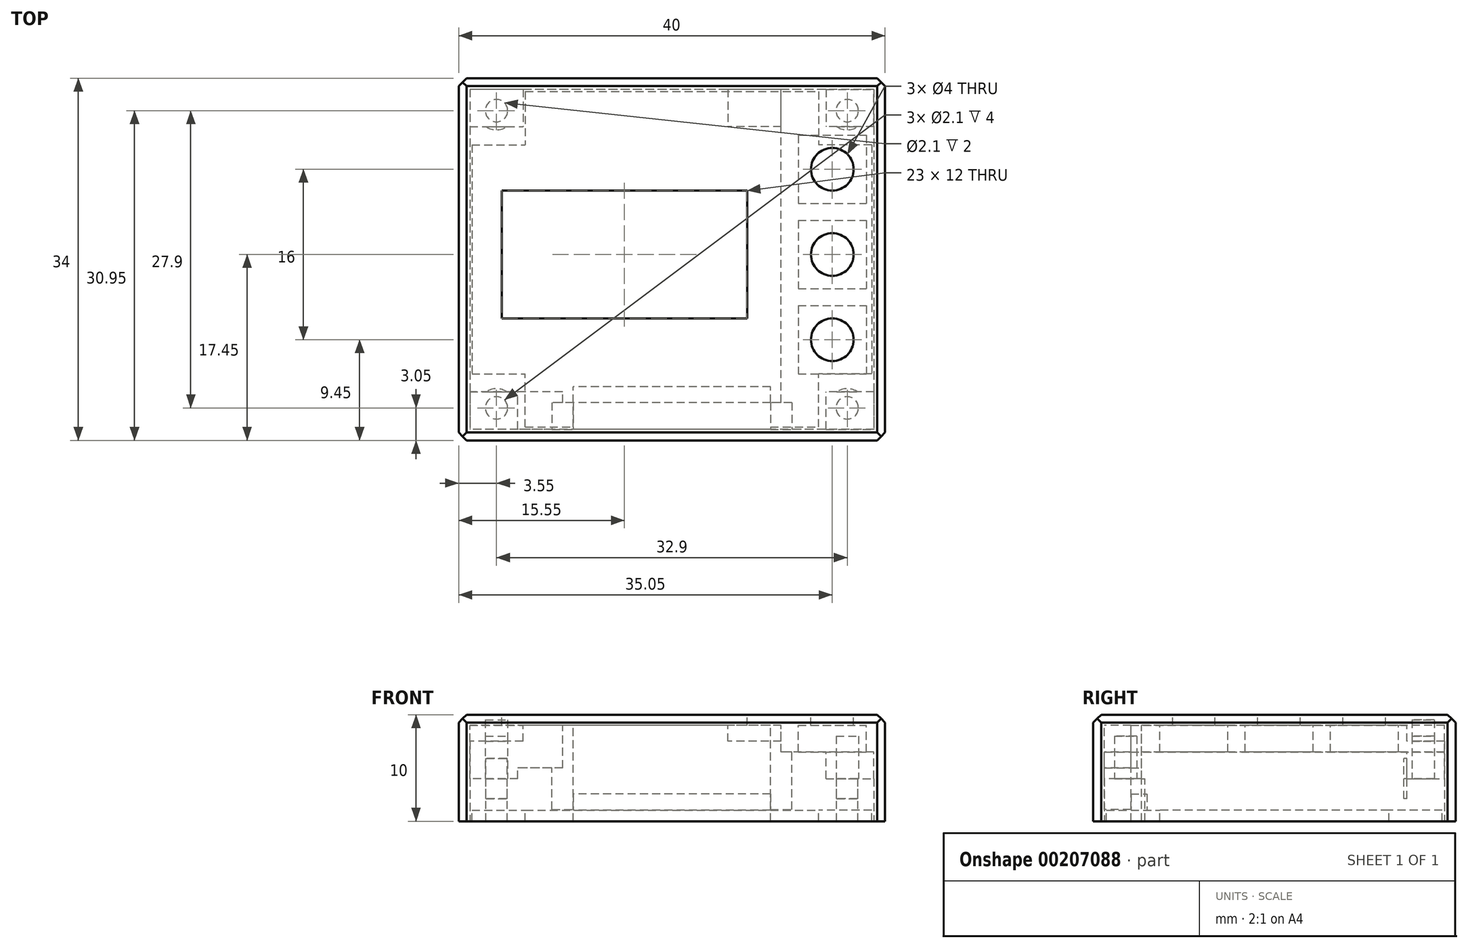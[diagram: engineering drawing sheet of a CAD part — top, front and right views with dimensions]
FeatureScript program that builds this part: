
annotation { "Feature Type Name" : "Feature", "Feature Type Description" : "" }
export const myFeature = defineFeature(function(context is Context, id is Id, definition is map)
    precondition{}
    {
        {
            var Q0;
            Q0=qCreatedBy(makeId("Top.planeOp"),FACE);
            var sketch = newSketch(context, id + "F0", { "sketchPlane" : qUnion([Q0])});
            skLineSegment(sketch, "E0.bottom", {"start": v(20, -17) * mm, "end": v(-20, -17) * mm});
            skLineSegment(sketch, "E0.top", {"start": v(20, 17) * mm, "end": v(-20, 17) * mm});
            skLineSegment(sketch, "E0.left", {"start": v(20, -17) * mm, "end": v(20, 17) * mm});
            skLineSegment(sketch, "E0.right", {"start": v(-20, -17) * mm, "end": v(-20, 17) * mm});
            skPoint(sketch, "E0.middle", {"position": v(0, 0) * mm});
            skSolve(sketch);
        }
        {
            var Q0;
            Q0=makeQuery(id+"F0.imprint","IMPRINT",FACE,{"disambiguationData":[TD([[makeQuery(id+"F0.imprint","IMPRINT",EDGE,{"derivedFrom":sQuery(id+"F0.wireOp",EDGE,"E0.bottom")}),-1.0]])]});
            extrude(context, id + "F1", {"entities" : qUnion([Q0]), "depth" : 10 * mm});
        }
        {
            var Q0;
            Q0=makeQuery(id+"F1.opExtrude","CAP_FACE",FACE,{"disambiguationData":[OSD([sQuery(id+"F0.wireOp",EDGE,"E0.bottom"),sQuery(id+"F0.wireOp",EDGE,"E0.top"),sQuery(id+"F0.wireOp",EDGE,"E0.left"),sQuery(id+"F0.wireOp",EDGE,"E0.right")])],"isStart":true});
            var sketch = newSketch(context, id + "F2", { "sketchPlane" : qUnion([Q0])});
            skLineSegment(sketch, "E1.bottom", {"start": v(18.95, -15.95) * mm, "end": v(-18.95, -15.95) * mm});
            skLineSegment(sketch, "E1.top", {"start": v(18.95, 15.95) * mm, "end": v(-18.95, 15.95) * mm});
            skLineSegment(sketch, "E1.left", {"start": v(18.95, -15.95) * mm, "end": v(18.95, 15.95) * mm});
            skLineSegment(sketch, "E1.right", {"start": v(-18.95, -15.95) * mm, "end": v(-18.95, 15.95) * mm});
            skPoint(sketch, "E1.middle", {"position": v(0, 0) * mm});
            skSolve(sketch);
        }
        {
            var Q0;
            Q0=makeQuery(id+"F2.imprint","IMPRINT",FACE,{"disambiguationData":[TD([[makeQuery(id+"F2.imprint","IMPRINT",EDGE,{"derivedFrom":sQuery(id+"F2.wireOp",EDGE,"E1.bottom")}),-1.0]])]});
            extrude(context, id + "F3", {"entities" : qUnion([Q0]), "operationType" : NewBodyOperationType.REMOVE, "oppositeDirection" : true, "depth" : 9 * mm});
        }
        {
            var Q0;
            Q0=makeQuery(id+"F1.opExtrude","CAP_FACE",FACE,{"disambiguationData":[OSD([sQuery(id+"F0.wireOp",EDGE,"E0.bottom"),sQuery(id+"F0.wireOp",EDGE,"E0.top"),sQuery(id+"F0.wireOp",EDGE,"E0.left"),sQuery(id+"F0.wireOp",EDGE,"E0.right")])],"isStart":false});
            var sketch = newSketch(context, id + "F4", { "sketchPlane" : qUnion([Q0])});
            skLineSegment(sketch, "E2.bottom", {"start": v(-15.95, 6.45) * mm, "end": v(7.05, 6.45) * mm});
            skLineSegment(sketch, "E2.top", {"start": v(-15.95, -5.55) * mm, "end": v(7.05, -5.55) * mm});
            skLineSegment(sketch, "E2.left", {"start": v(-15.95, 6.45) * mm, "end": v(-15.95, -5.55) * mm});
            skLineSegment(sketch, "E2.right", {"start": v(7.05, 6.45) * mm, "end": v(7.05, -5.55) * mm});
            skCircle(sketch, "E3", {"center": v(15.05, 0.45) * mm, "radius": 2 * mm});
            skPoint(sketch, "E3.centerSnap0", {"position": v(7.05, 0.45) * mm});
            skCircle(sketch, "E4", {"center": v(15.05, -7.55) * mm, "radius": 2 * mm});
            skCircle(sketch, "E5", {"center": v(15.05, 8.45) * mm, "radius": 2 * mm});
            skSolve(sketch);
        }
        {
            var Q0;
            Q0=makeQuery(id+"F4.imprint","IMPRINT",FACE,{"disambiguationData":[TD([[makeQuery(id+"F4.imprint","IMPRINT",EDGE,{"derivedFrom":sQuery(id+"F4.wireOp",EDGE,"E4")}),1.0]])]});
            var Q1;
            Q1=makeQuery(id+"F4.imprint","IMPRINT",FACE,{"disambiguationData":[TD([[makeQuery(id+"F4.imprint","IMPRINT",EDGE,{"derivedFrom":sQuery(id+"F4.wireOp",EDGE,"E3")}),1.0]])]});
            var Q2;
            Q2=makeQuery(id+"F4.imprint","IMPRINT",FACE,{"disambiguationData":[TD([[makeQuery(id+"F4.imprint","IMPRINT",EDGE,{"derivedFrom":sQuery(id+"F4.wireOp",EDGE,"E5")}),1.0]])]});
            var Q3;
            Q3=makeQuery(id+"F4.imprint","IMPRINT",FACE,{"disambiguationData":[TD([[makeQuery(id+"F4.imprint","IMPRINT",EDGE,{"derivedFrom":sQuery(id+"F4.wireOp",EDGE,"E2.bottom")}),-1.0]])]});
            extrude(context, id + "F5", {"entities" : qUnion([Q0, Q1, Q2, Q3]), "operationType" : NewBodyOperationType.REMOVE, "oppositeDirection" : true, "depth" : 25 * mm});
        }
        {
            var Q0;
            Q0=makeQuery(id+"F3.boolean.opBoolean","COPY",FACE,{"derivedFrom":makeQuery(id+"F3.opExtrude","CAP_FACE",FACE,{"disambiguationData":[OSD([sQuery(id+"F2.wireOp",EDGE,"E1.bottom"),sQuery(id+"F2.wireOp",EDGE,"E1.top"),sQuery(id+"F2.wireOp",EDGE,"E1.left"),sQuery(id+"F2.wireOp",EDGE,"E1.right")])],"isStart":false})});
            var sketch = newSketch(context, id + "F6", { "sketchPlane" : qUnion([Q0])});
            skLineSegment(sketch, "E6.bottom", {"start": v(11.85, 4.35) * mm, "end": v(18.25, 4.35) * mm});
            skLineSegment(sketch, "E6.top", {"start": v(11.85, 10.75) * mm, "end": v(18.25, 10.75) * mm});
            skLineSegment(sketch, "E6.left", {"start": v(11.85, 4.35) * mm, "end": v(11.85, 10.75) * mm});
            skLineSegment(sketch, "E6.right", {"start": v(18.25, 4.35) * mm, "end": v(18.25, 10.75) * mm});
            skPoint(sketch, "E6.middle", {"position": v(15.05, 7.55) * mm});
            skLineSegment(sketch, "E7.bottom", {"start": v(11.85, -3.65) * mm, "end": v(18.25, -3.65) * mm});
            skLineSegment(sketch, "E7.top", {"start": v(11.85, 2.75) * mm, "end": v(18.25, 2.75) * mm});
            skLineSegment(sketch, "E7.left", {"start": v(11.85, -3.65) * mm, "end": v(11.85, 2.75) * mm});
            skLineSegment(sketch, "E7.right", {"start": v(18.25, -3.65) * mm, "end": v(18.25, 2.75) * mm});
            skPoint(sketch, "E7.middle", {"position": v(15.05, -0.45) * mm});
            skLineSegment(sketch, "E8.bottom", {"start": v(11.85, -11.65) * mm, "end": v(18.25, -11.65) * mm});
            skLineSegment(sketch, "E8.top", {"start": v(11.85, -5.25) * mm, "end": v(18.25, -5.25) * mm});
            skLineSegment(sketch, "E8.left", {"start": v(11.85, -11.65) * mm, "end": v(11.85, -5.25) * mm});
            skLineSegment(sketch, "E8.right", {"start": v(18.25, -11.65) * mm, "end": v(18.25, -5.25) * mm});
            skPoint(sketch, "E8.middle", {"position": v(15.05, -8.45) * mm});
            skLineSegment(sketch, "E9", {"start": v(10.25, 15.95) * mm, "end": v(10.25, -15.95) * mm});
            skLineSegment(sketch, "E10", {"start": v(10.25, 12.45) * mm, "end": v(-18.95, 12.45) * mm});
            skLineSegment(sketch, "E11", {"start": v(-10.25, 15.95) * mm, "end": v(-10.25, 12.45) * mm});
            skLineSegment(sketch, "E12.bottom", {"start": v(-18.95, 12.45) * mm, "end": v(-13.95, 12.45) * mm});
            skLineSegment(sketch, "E12.top", {"start": v(-18.95, 8.95) * mm, "end": v(-13.95, 8.95) * mm});
            skLineSegment(sketch, "E12.left", {"start": v(-18.95, 12.45) * mm, "end": v(-18.95, 8.95) * mm});
            skLineSegment(sketch, "E12.right", {"start": v(-13.95, 12.45) * mm, "end": v(-13.95, 8.95) * mm});
            skLineSegment(sketch, "E13.bottom", {"start": v(-18.95, -15.95) * mm, "end": v(-13.95, -15.95) * mm});
            skLineSegment(sketch, "E13.top", {"start": v(-18.95, -12.45) * mm, "end": v(-13.95, -12.45) * mm});
            skLineSegment(sketch, "E13.left", {"start": v(-18.95, -15.95) * mm, "end": v(-18.95, -12.45) * mm});
            skLineSegment(sketch, "E13.right", {"start": v(-13.95, -15.95) * mm, "end": v(-13.95, -12.45) * mm});
            skLineSegment(sketch, "E14.bottom", {"start": v(10.25, -15.95) * mm, "end": v(5.25, -15.95) * mm});
            skLineSegment(sketch, "E14.top", {"start": v(10.25, -12.45) * mm, "end": v(5.25, -12.45) * mm});
            skLineSegment(sketch, "E14.left", {"start": v(10.25, -15.95) * mm, "end": v(10.25, -12.45) * mm});
            skLineSegment(sketch, "E14.right", {"start": v(5.25, -15.95) * mm, "end": v(5.25, -12.45) * mm});
            skLineSegment(sketch, "E15.bottom", {"start": v(10.25, 12.45) * mm, "end": v(5.25, 12.45) * mm});
            skLineSegment(sketch, "E15.top", {"start": v(10.25, 8.95) * mm, "end": v(5.25, 8.95) * mm});
            skLineSegment(sketch, "E15.left", {"start": v(10.25, 12.45) * mm, "end": v(10.25, 8.95) * mm});
            skLineSegment(sketch, "E15.right", {"start": v(5.25, 12.45) * mm, "end": v(5.25, 8.95) * mm});
            skSolve(sketch);
        }
        {
            var Q0;
            Q0=makeQuery(id+"F6.imprint","IMPRINT",FACE,{"disambiguationData":[TD([[makeQuery(id+"F6.imprint","IMPRINT",EDGE,{"derivedFrom":sQuery(id+"F6.wireOp",EDGE,"E6.bottom")}),-1.0]])]});
            extrude(context, id + "F7", {"entities" : qUnion([Q0]), "operationType" : NewBodyOperationType.ADD, "depth" : 2.5 * mm});
        }
        {
            var Q0;
            Q0=makeQuery(id+"F6.imprint","IMPRINT",FACE,{"disambiguationData":[TD([[makeQuery(id+"F6.imprint","IMPRINT",EDGE,{"derivedFrom":sQuery(id+"F6.wireOp",EDGE,"E12.bottom")}),-1.0]])]});
            var Q1;
            Q1=makeQuery(id+"F6.imprint","IMPRINT",FACE,{"disambiguationData":[TD([[makeQuery(id+"F6.imprint","IMPRINT",EDGE,{"derivedFrom":sQuery(id+"F6.wireOp",EDGE,"E15.bottom")}),1.0]])]});
            var Q2;
            Q2=makeQuery(id+"F6.imprint","IMPRINT",FACE,{"disambiguationData":[TD([[makeQuery(id+"F6.imprint","IMPRINT",EDGE,{"derivedFrom":sQuery(id+"F6.wireOp",EDGE,"E13.bottom")}),-1.0]])]});
            var Q3;
            Q3=makeQuery(id+"F6.imprint","IMPRINT",FACE,{"disambiguationData":[TD([[makeQuery(id+"F6.imprint","IMPRINT",EDGE,{"derivedFrom":sQuery(id+"F6.wireOp",EDGE,"E14.bottom")}),-1.0]])]});
            extrude(context, id + "F8", {"entities" : qUnion([Q0, Q1, Q2, Q3]), "operationType" : NewBodyOperationType.ADD, "depth" : 1.5 * mm});
        }
        {
            var Q0;
            {var subQ3=sQuery(id+"F6.wireOp",EDGE,"E11");Q0=makeQuery(id+"F6.imprint","IMPRINT",FACE,{"disambiguationData":[TD([[makeQuery(id+"F6.imprint","IMPRINT",EDGE,{"derivedFrom":subQ3}),-1.0]])]});}
            extrude(context, id + "F9", {"entities" : qUnion([Q0]), "operationType" : NewBodyOperationType.ADD, "depth" : 4 * mm});
        }
        {
            var Q0;
            Q0=makeQuery(id+"F8.opExtrude","CAP_FACE",FACE,{"disambiguationData":[OSD([sQuery(id+"F6.wireOp",EDGE,"E13.bottom"),sQuery(id+"F6.wireOp",EDGE,"E13.top"),sQuery(id+"F6.wireOp",EDGE,"E13.left"),sQuery(id+"F6.wireOp",EDGE,"E13.right")])],"isStart":false});
            var sketch = newSketch(context, id + "F10", { "sketchPlane" : qUnion([Q0])});
            skCircle(sketch, "E16", {"center": v(-16.45, -13.95) * mm, "radius": 1.05 * mm});
            skSolve(sketch);
        }
        {
            var Q0;
            Q0=makeQuery(id+"F10.imprint","IMPRINT",FACE,{"disambiguationData":[TD([[makeQuery(id+"F10.imprint","IMPRINT",EDGE,{"derivedFrom":sQuery(id+"F10.wireOp",EDGE,"E16")}),1.0]])]});
            extrude(context, id + "F11", {"entities" : qUnion([Q0]), "operationType" : NewBodyOperationType.REMOVE, "oppositeDirection" : true, "depth" : 2 * mm});
        }
        {
            var Q0;
            Q0=makeQuery(id+"F1.opExtrude","CAP_EDGE",EDGE,{"disambiguationData":[OSD([sQuery(id+"F0.wireOp",EDGE,"E0.right")])],"isStart":false});
            var Q1;
            Q1=makeQuery(id+"F1.opExtrude","CAP_EDGE",EDGE,{"disambiguationData":[OSD([sQuery(id+"F0.wireOp",EDGE,"E0.top")])],"isStart":false});
            var Q2;
            Q2=makeQuery(id+"F1.opExtrude","CAP_EDGE",EDGE,{"disambiguationData":[OSD([sQuery(id+"F0.wireOp",EDGE,"E0.left")])],"isStart":false});
            var Q3;
            Q3=makeQuery(id+"F1.opExtrude","CAP_EDGE",EDGE,{"disambiguationData":[OSD([sQuery(id+"F0.wireOp",EDGE,"E0.bottom")])],"isStart":false});
            var Q4;
            Q4=makeQuery(id+"F5.boolean.opBoolean","COPY",EDGE,{"derivedFrom":makeQuery(id+"F5.opExtrude","CAP_EDGE",EDGE,{"disambiguationData":[OSD([sQuery(id+"F4.wireOp",EDGE,"E2.bottom")])],"isStart":true})});
            var Q5;
            Q5=makeQuery(id+"F5.boolean.opBoolean","COPY",EDGE,{"derivedFrom":makeQuery(id+"F5.opExtrude","CAP_EDGE",EDGE,{"disambiguationData":[OSD([sQuery(id+"F4.wireOp",EDGE,"E2.right")])],"isStart":true})});
            var Q6;
            Q6=makeQuery(id+"F5.boolean.opBoolean","COPY",EDGE,{"derivedFrom":makeQuery(id+"F5.opExtrude","CAP_EDGE",EDGE,{"disambiguationData":[OSD([sQuery(id+"F4.wireOp",EDGE,"E2.top")])],"isStart":true})});
            var Q7;
            Q7=makeQuery(id+"F5.boolean.opBoolean","COPY",EDGE,{"derivedFrom":makeQuery(id+"F5.opExtrude","CAP_EDGE",EDGE,{"disambiguationData":[OSD([sQuery(id+"F4.wireOp",EDGE,"E2.left")])],"isStart":true})});
            var Q8;
            Q8=makeQuery(id+"F5.boolean.opBoolean","COPY",EDGE,{"derivedFrom":makeQuery(id+"F5.opExtrude","CAP_EDGE",EDGE,{"disambiguationData":[OSD([sQuery(id+"F4.wireOp",EDGE,"E5")])],"isStart":true})});
            var Q9;
            Q9=makeQuery(id+"F5.boolean.opBoolean","COPY",EDGE,{"derivedFrom":makeQuery(id+"F5.opExtrude","CAP_EDGE",EDGE,{"disambiguationData":[OSD([sQuery(id+"F4.wireOp",EDGE,"E3")])],"isStart":true})});
            var Q10;
            Q10=makeQuery(id+"F5.boolean.opBoolean","COPY",EDGE,{"derivedFrom":makeQuery(id+"F5.opExtrude","CAP_EDGE",EDGE,{"disambiguationData":[OSD([sQuery(id+"F4.wireOp",EDGE,"E4")])],"isStart":true})});
            chamfer(context, id + "F12", {"entities" : qUnion([Q0, Q1, Q2, Q3, Q4, Q5, Q6, Q7, Q8, Q9, Q10]), "width" : 0.75 * mm, "tangentPropagation" : true});
        }
        {
            var Q0;
            Q0=makeQuery(id+"F3.boolean.opBoolean","COPY",FACE,{"derivedFrom":makeQuery(id+"F3.opExtrude","SWEPT_FACE",FACE,{"disambiguationData":[OSD([sQuery(id+"F2.wireOp",EDGE,"E1.top")])]})});
            var sketch = newSketch(context, id + "F13", { "sketchPlane" : qUnion([Q0])});
            skLineSegment(sketch, "E17", {"start": v(11.25, 0) * mm, "end": v(11.25, 9) * mm});
            skLineSegment(sketch, "E18", {"start": v(9.25, 0) * mm, "end": v(9.25, 9) * mm});
            skLineSegment(sketch, "E19.bottom", {"start": v(-9.25, 0) * mm, "end": v(-11.25, 0) * mm});
            skLineSegment(sketch, "E19.top", {"start": v(-9.25, 9) * mm, "end": v(-11.25, 9) * mm});
            skLineSegment(sketch, "E19.left", {"start": v(-9.25, 0) * mm, "end": v(-9.25, 9) * mm});
            skLineSegment(sketch, "E19.right", {"start": v(-11.25, 0) * mm, "end": v(-11.25, 9) * mm});
            skSolve(sketch);
        }
        {
            var Q0;
            {var subQ4=sQuery(id+"F13.wireOp",EDGE,"E18");Q0=makeQuery(id+"F13.imprint","IMPRINT",FACE,{"disambiguationData":[TD([[makeQuery(id+"F13.imprint","IMPRINT",EDGE,{"derivedFrom":subQ4}),-1.0]])]});}
            var Q1;
            {var subQ1=sQuery(id+"F13.wireOp",EDGE,"E19.bottom");Q1=makeQuery(id+"F13.imprint","IMPRINT",FACE,{"disambiguationData":[TD([[makeQuery(id+"F13.imprint","IMPRINT",EDGE,{"derivedFrom":subQ1}),1.0]])]});}
            extrude(context, id + "F14", {"entities" : qUnion([Q0, Q1]), "operationType" : NewBodyOperationType.ADD, "depth" : 2.5 * mm});
        }
        {
            var Q0;
            {var subQ0=sQuery(id+"F2.wireOp",EDGE,"E1.top");var subQ1=makeQuery(id+"F3.boolean.opBoolean","COPY",EDGE,{"derivedFrom":makeQuery(id+"F3.opExtrude","CAP_EDGE",EDGE,{"disambiguationData":[OSD([subQ0])],"isStart":true})});Q0=makeQuery(id+"F14.boolean.opBoolean","MERGE",FACE,{"derivedFrom":[makeQuery(id+"F1.opExtrude","CAP_FACE",FACE,{"disambiguationData":[OSD([sQuery(id+"F0.wireOp",EDGE,"E0.bottom"),sQuery(id+"F0.wireOp",EDGE,"E0.top"),sQuery(id+"F0.wireOp",EDGE,"E0.left"),sQuery(id+"F0.wireOp",EDGE,"E0.right")])],"isStart":true}),makeQuery(id+"F14.opExtrude","SWEPT_FACE",FACE,{"disambiguationData":[OSD([sQuery(id+"F13.wireOp",EDGE,"E19.bottom")])]}),makeQuery(id+"F14.opExtrude","SWEPT_FACE",FACE,{"disambiguationData":[OSD([subQ0]),TDD([makeQuery(id+"F13.imprint","IMPRINT",EDGE,{"disambiguationData":[TD([[makeQuery(id+"F13.imprint","INTERSECT",VERTEX,{"derivedFrom":[subQ1,sQuery(id+"F13.wireOp",EDGE,"E17")]}),1.0]])],"derivedFrom":subQ1})])]})]});}
            var sketch = newSketch(context, id + "F15", { "sketchPlane" : qUnion([Q0])});
            skLineSegment(sketch, "E20", {"start": v(-11.25, 15.95) * mm, "end": v(-9.25, 15.95) * mm});
            skLineSegment(sketch, "E21", {"start": v(9.25, 15.95) * mm, "end": v(11.25, 15.95) * mm});
            skSolve(sketch);
        }
        {
            var Q0;
            Q0=makeQuery(id+"F15.imprint","IMPRINT",FACE,{"disambiguationData":[TD([[makeQuery(id+"F15.imprint","IMPRINT",EDGE,{"derivedFrom":sQuery(id+"F15.wireOp",EDGE,"E20")}),-1.0]])]});
            var Q1;
            Q1=makeQuery(id+"F15.imprint","IMPRINT",FACE,{"disambiguationData":[TD([[makeQuery(id+"F15.imprint","IMPRINT",EDGE,{"derivedFrom":sQuery(id+"F15.wireOp",EDGE,"E21")}),-1.0]])]});
            extrude(context, id + "F16", {"entities" : qUnion([Q0, Q1]), "operationType" : NewBodyOperationType.REMOVE, "oppositeDirection" : true, "depth" : 1.1 * mm});
        }
        {
            var Q0;
            Q0=makeQuery(id+"F1.opExtrude","SWEPT_EDGE",EDGE,{"disambiguationData":[OSD([sQuery(id+"F0.wireOp",EDGE,"E0.top"),sQuery(id+"F0.wireOp",EDGE,"E0.right")])]});
            var Q1;
            Q1=makeQuery(id+"F1.opExtrude","SWEPT_EDGE",EDGE,{"disambiguationData":[OSD([sQuery(id+"F0.wireOp",EDGE,"E0.top"),sQuery(id+"F0.wireOp",EDGE,"E0.left")])]});
            var Q2;
            Q2=makeQuery(id+"F1.opExtrude","SWEPT_EDGE",EDGE,{"disambiguationData":[OSD([sQuery(id+"F0.wireOp",EDGE,"E0.bottom"),sQuery(id+"F0.wireOp",EDGE,"E0.right")])]});
            var Q3;
            Q3=makeQuery(id+"F1.opExtrude","SWEPT_EDGE",EDGE,{"disambiguationData":[OSD([sQuery(id+"F0.wireOp",EDGE,"E0.bottom"),sQuery(id+"F0.wireOp",EDGE,"E0.left")])]});
            chamfer(context, id + "F17", {"entities" : qUnion([Q0, Q1, Q2, Q3]), "width" : 0.75 * mm, "tangentPropagation" : true});
        }
        {
            var Q0;
            Q0=makeQuery(id+"F9.opExtrude","CAP_FACE",FACE,{"disambiguationData":[OSD([sQuery(id+"F2.wireOp",EDGE,"E1.top"),sQuery(id+"F2.wireOp",EDGE,"E1.right"),sQuery(id+"F6.wireOp",EDGE,"E10"),sQuery(id+"F6.wireOp",EDGE,"E11"),sQuery(id+"F6.wireOp",EDGE,"E12.bottom")])],"isStart":false});
            var sketch = newSketch(context, id + "F18", { "sketchPlane" : qUnion([Q0])});
            skLineSegment(sketch, "E22.bottom", {"start": v(-18.95, 15.95) * mm, "end": v(-14.45, 15.95) * mm});
            skLineSegment(sketch, "E22.top", {"start": v(-18.95, 12.45) * mm, "end": v(-14.45, 12.45) * mm});
            skLineSegment(sketch, "E22.left", {"start": v(-18.95, 15.95) * mm, "end": v(-18.95, 12.45) * mm});
            skLineSegment(sketch, "E22.right", {"start": v(-14.45, 15.95) * mm, "end": v(-14.45, 12.45) * mm});
            skSolve(sketch);
        }
        {
            var Q0;
            Q0=makeQuery(id+"F7.opExtrude","CAP_FACE",FACE,{"disambiguationData":[OSD([sQuery(id+"F2.wireOp",EDGE,"E1.bottom"),sQuery(id+"F2.wireOp",EDGE,"E1.top"),sQuery(id+"F2.wireOp",EDGE,"E1.left"),sQuery(id+"F6.wireOp",EDGE,"E6.bottom"),sQuery(id+"F6.wireOp",EDGE,"E6.top"),sQuery(id+"F6.wireOp",EDGE,"E6.left"),sQuery(id+"F6.wireOp",EDGE,"E6.right"),sQuery(id+"F6.wireOp",EDGE,"E7.bottom"),sQuery(id+"F6.wireOp",EDGE,"E7.top"),sQuery(id+"F6.wireOp",EDGE,"E7.left"),sQuery(id+"F6.wireOp",EDGE,"E7.right"),sQuery(id+"F6.wireOp",EDGE,"E8.bottom"),sQuery(id+"F6.wireOp",EDGE,"E8.top"),sQuery(id+"F6.wireOp",EDGE,"E8.left"),sQuery(id+"F6.wireOp",EDGE,"E8.right"),sQuery(id+"F6.wireOp",EDGE,"E9"),sQuery(id+"F6.wireOp",EDGE,"E14.left"),sQuery(id+"F6.wireOp",EDGE,"E15.left")])],"isStart":false});
            var sketch = newSketch(context, id + "F19", { "sketchPlane" : qUnion([Q0])});
            skLineSegment(sketch, "E23.bottom", {"start": v(18.95, 15.95) * mm, "end": v(14.45, 15.95) * mm});
            skLineSegment(sketch, "E23.top", {"start": v(18.95, 12.45) * mm, "end": v(14.45, 12.45) * mm});
            skLineSegment(sketch, "E23.left", {"start": v(18.95, 15.95) * mm, "end": v(18.95, 12.45) * mm});
            skLineSegment(sketch, "E23.right", {"start": v(14.45, 15.95) * mm, "end": v(14.45, 12.45) * mm});
            skLineSegment(sketch, "E24.bottom", {"start": v(18.95, -15.95) * mm, "end": v(14.45, -15.95) * mm});
            skLineSegment(sketch, "E24.top", {"start": v(18.95, -12.45) * mm, "end": v(14.45, -12.45) * mm});
            skLineSegment(sketch, "E24.left", {"start": v(18.95, -15.95) * mm, "end": v(18.95, -12.45) * mm});
            skLineSegment(sketch, "E24.right", {"start": v(14.45, -15.95) * mm, "end": v(14.45, -12.45) * mm});
            skSolve(sketch);
        }
        {
            var Q0;
            Q0=makeQuery(id+"F18.imprint","IMPRINT",FACE,{"disambiguationData":[TD([[makeQuery(id+"F18.imprint","IMPRINT",EDGE,{"derivedFrom":sQuery(id+"F18.wireOp",EDGE,"E22.bottom")}),1.0]])]});
            var Q1;
            Q1=makeQuery(id+"F19.imprint","IMPRINT",FACE,{"disambiguationData":[TD([[makeQuery(id+"F19.imprint","IMPRINT",EDGE,{"derivedFrom":sQuery(id+"F19.wireOp",EDGE,"E23.bottom")}),1.0]])]});
            var Q2;
            Q2=makeQuery(id+"F19.imprint","IMPRINT",FACE,{"disambiguationData":[TD([[makeQuery(id+"F19.imprint","IMPRINT",EDGE,{"derivedFrom":sQuery(id+"F19.wireOp",EDGE,"E24.bottom")}),-1.0]])]});
            var Q3;
            {var subQ0=sQuery(id+"F2.wireOp",EDGE,"E1.top");var subQ1=makeQuery(id+"F3.boolean.opBoolean","COPY",EDGE,{"derivedFrom":makeQuery(id+"F3.opExtrude","CAP_EDGE",EDGE,{"disambiguationData":[OSD([subQ0])],"isStart":true})});Q3=makeQuery(id+"F14.boolean.opBoolean","MERGE",FACE,{"derivedFrom":[makeQuery(id+"F1.opExtrude","CAP_FACE",FACE,{"disambiguationData":[OSD([sQuery(id+"F0.wireOp",EDGE,"E0.bottom"),sQuery(id+"F0.wireOp",EDGE,"E0.top"),sQuery(id+"F0.wireOp",EDGE,"E0.left"),sQuery(id+"F0.wireOp",EDGE,"E0.right")])],"isStart":true}),makeQuery(id+"F14.opExtrude","SWEPT_FACE",FACE,{"disambiguationData":[OSD([sQuery(id+"F13.wireOp",EDGE,"E19.bottom")])]}),makeQuery(id+"F14.opExtrude","SWEPT_FACE",FACE,{"disambiguationData":[OSD([subQ0]),TDD([makeQuery(id+"F13.imprint","IMPRINT",EDGE,{"disambiguationData":[TD([[makeQuery(id+"F13.imprint","INTERSECT",VERTEX,{"derivedFrom":[subQ1,sQuery(id+"F13.wireOp",EDGE,"E17")]}),1.0]])],"derivedFrom":subQ1})])]})]});}
            extrude(context, id + "F20", {"entities" : qUnion([Q0, Q1, Q2]), "operationType" : NewBodyOperationType.ADD, "endBound" : BoundingType.UP_TO_SURFACE, "endBoundEntityFace" : qUnion([Q3]), "depth" : 25 * mm});
        }
        {
            var Q0;
            {var subQ0=sQuery(id+"F13.wireOp",EDGE,"E19.bottom");var subQ1=sQuery(id+"F2.wireOp",EDGE,"E1.top");var subQ2=sQuery(id+"F0.wireOp",EDGE,"E0.right");var subQ3=sQuery(id+"F0.wireOp",EDGE,"E0.left");var subQ4=sQuery(id+"F0.wireOp",EDGE,"E0.top");var subQ5=sQuery(id+"F0.wireOp",EDGE,"E0.bottom");var subQ6=makeQuery(id+"F3.boolean.opBoolean","COPY",EDGE,{"derivedFrom":makeQuery(id+"F3.opExtrude","CAP_EDGE",EDGE,{"disambiguationData":[OSD([subQ1])],"isStart":true})});Q0=makeQuery(id+"F20.boolean.opBoolean","MERGE",FACE,{"derivedFrom":[makeQuery(id+"F14.boolean.opBoolean","MERGE",FACE,{"derivedFrom":[makeQuery(id+"F1.opExtrude","CAP_FACE",FACE,{"disambiguationData":[OSD([subQ5,subQ4,subQ3,subQ2])],"isStart":true}),makeQuery(id+"F14.opExtrude","SWEPT_FACE",FACE,{"disambiguationData":[OSD([subQ0])]}),makeQuery(id+"F14.opExtrude","SWEPT_FACE",FACE,{"disambiguationData":[OSD([subQ1]),TDD([makeQuery(id+"F13.imprint","IMPRINT",EDGE,{"disambiguationData":[TD([[makeQuery(id+"F13.imprint","INTERSECT",VERTEX,{"derivedFrom":[subQ6,sQuery(id+"F13.wireOp",EDGE,"E17")]}),1.0]])],"derivedFrom":subQ6})])]})]}),makeQuery(id+"F20.opExtrude","CAP_FACE",FACE,{"disambiguationData":[OSD([subQ5,subQ4,subQ3,subQ2,subQ1,subQ0]),ownerDisambiguation([makeQuery(id+"F20.opExtrude","SWEPT_BODY",BODY,{"disambiguationData":[OSD([sQuery(id+"F18.wireOp",EDGE,"E22.bottom"),sQuery(id+"F18.wireOp",EDGE,"E22.top"),sQuery(id+"F18.wireOp",EDGE,"E22.left"),sQuery(id+"F18.wireOp",EDGE,"E22.right")])]})])],"isStart":false}),makeQuery(id+"F20.opExtrude","CAP_FACE",FACE,{"disambiguationData":[OSD([subQ5,subQ4,subQ3,subQ2,subQ1,subQ0]),ownerDisambiguation([makeQuery(id+"F20.opExtrude","SWEPT_BODY",BODY,{"disambiguationData":[OSD([sQuery(id+"F19.wireOp",EDGE,"E23.bottom"),sQuery(id+"F19.wireOp",EDGE,"E23.top"),sQuery(id+"F19.wireOp",EDGE,"E23.left"),sQuery(id+"F19.wireOp",EDGE,"E23.right")])]})])],"isStart":false}),makeQuery(id+"F20.opExtrude","CAP_FACE",FACE,{"disambiguationData":[OSD([subQ5,subQ4,subQ3,subQ2,subQ1,subQ0]),ownerDisambiguation([makeQuery(id+"F20.opExtrude","SWEPT_BODY",BODY,{"disambiguationData":[OSD([sQuery(id+"F19.wireOp",EDGE,"E24.bottom"),sQuery(id+"F19.wireOp",EDGE,"E24.top"),sQuery(id+"F19.wireOp",EDGE,"E24.left"),sQuery(id+"F19.wireOp",EDGE,"E24.right")])]})])],"isStart":false})]});}
            var sketch = newSketch(context, id + "F21", { "sketchPlane" : qUnion([Q0])});
            skLineSegment(sketch, "E25.bottom", {"start": v(-14.45, 12.45) * mm, "end": v(-18.95, 12.45) * mm});
            skLineSegment(sketch, "E25.top", {"start": v(-14.45, 15.95) * mm, "end": v(-18.95, 15.95) * mm});
            skLineSegment(sketch, "E25.left", {"start": v(-14.45, 12.45) * mm, "end": v(-14.45, 15.95) * mm});
            skLineSegment(sketch, "E25.right", {"start": v(-18.95, 12.45) * mm, "end": v(-18.95, 15.95) * mm});
            skLineSegment(sketch, "E26.bottom", {"start": v(14.45, 12.45) * mm, "end": v(18.95, 12.45) * mm});
            skLineSegment(sketch, "E26.top", {"start": v(14.45, 15.95) * mm, "end": v(18.95, 15.95) * mm});
            skLineSegment(sketch, "E26.left", {"start": v(14.45, 12.45) * mm, "end": v(14.45, 15.95) * mm});
            skLineSegment(sketch, "E26.right", {"start": v(18.95, 12.45) * mm, "end": v(18.95, 15.95) * mm});
            skLineSegment(sketch, "E27.bottom", {"start": v(14.45, -12.45) * mm, "end": v(18.95, -12.45) * mm});
            skLineSegment(sketch, "E27.top", {"start": v(14.45, -15.95) * mm, "end": v(18.95, -15.95) * mm});
            skLineSegment(sketch, "E27.left", {"start": v(14.45, -12.45) * mm, "end": v(14.45, -15.95) * mm});
            skLineSegment(sketch, "E27.right", {"start": v(18.95, -12.45) * mm, "end": v(18.95, -15.95) * mm});
            skSolve(sketch);
        }
        {
            var Q0;
            Q0=makeQuery(id+"F21.imprint","IMPRINT",FACE,{"disambiguationData":[TD([[makeQuery(id+"F21.imprint","IMPRINT",EDGE,{"derivedFrom":sQuery(id+"F21.wireOp",EDGE,"E25.bottom")}),1.0]])]});
            var Q1;
            Q1=makeQuery(id+"F21.imprint","IMPRINT",FACE,{"disambiguationData":[TD([[makeQuery(id+"F21.imprint","IMPRINT",EDGE,{"derivedFrom":sQuery(id+"F21.wireOp",EDGE,"E26.bottom")}),1.0]])]});
            var Q2;
            Q2=makeQuery(id+"F21.imprint","IMPRINT",FACE,{"disambiguationData":[TD([[makeQuery(id+"F21.imprint","IMPRINT",EDGE,{"derivedFrom":sQuery(id+"F21.wireOp",EDGE,"E27.bottom")}),-1.0]])]});
            extrude(context, id + "F22", {"entities" : qUnion([Q0, Q1, Q2]), "operationType" : NewBodyOperationType.REMOVE, "oppositeDirection" : true, "depth" : 4 * mm});
        }
        {
            var Q0;
            Q0=makeQuery(id+"F22.boolean.opBoolean","COPY",FACE,{"derivedFrom":makeQuery(id+"F22.opExtrude","CAP_FACE",FACE,{"disambiguationData":[OSD([sQuery(id+"F21.wireOp",EDGE,"E25.bottom"),sQuery(id+"F21.wireOp",EDGE,"E25.top"),sQuery(id+"F21.wireOp",EDGE,"E25.left"),sQuery(id+"F21.wireOp",EDGE,"E25.right")])],"isStart":false})});
            var sketch = newSketch(context, id + "F23", { "sketchPlane" : qUnion([Q0])});
            skCircle(sketch, "E28", {"center": v(-16.45, 13.95) * mm, "radius": 1.05 * mm});
            skSolve(sketch);
        }
        {
            var Q0;
            Q0=makeQuery(id+"F22.boolean.opBoolean","COPY",FACE,{"derivedFrom":makeQuery(id+"F22.opExtrude","CAP_FACE",FACE,{"disambiguationData":[OSD([sQuery(id+"F21.wireOp",EDGE,"E26.bottom"),sQuery(id+"F21.wireOp",EDGE,"E26.top"),sQuery(id+"F21.wireOp",EDGE,"E26.left"),sQuery(id+"F21.wireOp",EDGE,"E26.right")])],"isStart":false})});
            var sketch = newSketch(context, id + "F24", { "sketchPlane" : qUnion([Q0])});
            skCircle(sketch, "E29", {"center": v(16.45, 13.95) * mm, "radius": 1.05 * mm});
            skSolve(sketch);
        }
        {
            var Q0;
            Q0=makeQuery(id+"F22.boolean.opBoolean","COPY",FACE,{"derivedFrom":makeQuery(id+"F22.opExtrude","CAP_FACE",FACE,{"disambiguationData":[OSD([sQuery(id+"F21.wireOp",EDGE,"E27.bottom"),sQuery(id+"F21.wireOp",EDGE,"E27.top"),sQuery(id+"F21.wireOp",EDGE,"E27.left"),sQuery(id+"F21.wireOp",EDGE,"E27.right")])],"isStart":false})});
            var sketch = newSketch(context, id + "F25", { "sketchPlane" : qUnion([Q0])});
            skCircle(sketch, "E30", {"center": v(16.45, -13.95) * mm, "radius": 1.05 * mm});
            skSolve(sketch);
        }
        {
            var Q0;
            Q0=makeQuery(id+"F23.imprint","IMPRINT",FACE,{"disambiguationData":[TD([[makeQuery(id+"F23.imprint","IMPRINT",EDGE,{"derivedFrom":sQuery(id+"F23.wireOp",EDGE,"E28")}),1.0]])]});
            var Q1;
            Q1=makeQuery(id+"F24.imprint","IMPRINT",FACE,{"disambiguationData":[TD([[makeQuery(id+"F24.imprint","IMPRINT",EDGE,{"derivedFrom":sQuery(id+"F24.wireOp",EDGE,"E29")}),1.0]])]});
            var Q2;
            Q2=makeQuery(id+"F25.imprint","IMPRINT",FACE,{"disambiguationData":[TD([[makeQuery(id+"F25.imprint","IMPRINT",EDGE,{"derivedFrom":sQuery(id+"F25.wireOp",EDGE,"E30")}),1.0]])]});
            extrude(context, id + "F26", {"entities" : qUnion([Q0, Q1, Q2]), "operationType" : NewBodyOperationType.REMOVE, "oppositeDirection" : true, "depth" : 4 * mm});
        }
        {
            var Q0;
            {var subQ0=sQuery(id+"F13.wireOp",EDGE,"E19.bottom");var subQ1=sQuery(id+"F2.wireOp",EDGE,"E1.top");var subQ2=sQuery(id+"F0.wireOp",EDGE,"E0.right");var subQ3=sQuery(id+"F0.wireOp",EDGE,"E0.left");var subQ4=sQuery(id+"F0.wireOp",EDGE,"E0.top");var subQ5=sQuery(id+"F0.wireOp",EDGE,"E0.bottom");var subQ6=makeQuery(id+"F3.boolean.opBoolean","COPY",EDGE,{"derivedFrom":makeQuery(id+"F3.opExtrude","CAP_EDGE",EDGE,{"disambiguationData":[OSD([subQ1])],"isStart":true})});Q0=makeQuery(id+"F20.boolean.opBoolean","MERGE",FACE,{"derivedFrom":[makeQuery(id+"F14.boolean.opBoolean","MERGE",FACE,{"derivedFrom":[makeQuery(id+"F1.opExtrude","CAP_FACE",FACE,{"disambiguationData":[OSD([subQ5,subQ4,subQ3,subQ2])],"isStart":true}),makeQuery(id+"F14.opExtrude","SWEPT_FACE",FACE,{"disambiguationData":[OSD([subQ0])]}),makeQuery(id+"F14.opExtrude","SWEPT_FACE",FACE,{"disambiguationData":[OSD([subQ1]),TDD([makeQuery(id+"F13.imprint","IMPRINT",EDGE,{"disambiguationData":[TD([[makeQuery(id+"F13.imprint","INTERSECT",VERTEX,{"derivedFrom":[subQ6,sQuery(id+"F13.wireOp",EDGE,"E17")]}),1.0]])],"derivedFrom":subQ6})])]})]}),makeQuery(id+"F20.opExtrude","CAP_FACE",FACE,{"disambiguationData":[OSD([subQ5,subQ4,subQ3,subQ2,subQ1,subQ0]),ownerDisambiguation([makeQuery(id+"F20.opExtrude","SWEPT_BODY",BODY,{"disambiguationData":[OSD([sQuery(id+"F18.wireOp",EDGE,"E22.bottom"),sQuery(id+"F18.wireOp",EDGE,"E22.top"),sQuery(id+"F18.wireOp",EDGE,"E22.left"),sQuery(id+"F18.wireOp",EDGE,"E22.right")])]})])],"isStart":false}),makeQuery(id+"F20.opExtrude","CAP_FACE",FACE,{"disambiguationData":[OSD([subQ5,subQ4,subQ3,subQ2,subQ1,subQ0]),ownerDisambiguation([makeQuery(id+"F20.opExtrude","SWEPT_BODY",BODY,{"disambiguationData":[OSD([sQuery(id+"F19.wireOp",EDGE,"E23.bottom"),sQuery(id+"F19.wireOp",EDGE,"E23.top"),sQuery(id+"F19.wireOp",EDGE,"E23.left"),sQuery(id+"F19.wireOp",EDGE,"E23.right")])]})])],"isStart":false}),makeQuery(id+"F20.opExtrude","CAP_FACE",FACE,{"disambiguationData":[OSD([subQ5,subQ4,subQ3,subQ2,subQ1,subQ0]),ownerDisambiguation([makeQuery(id+"F20.opExtrude","SWEPT_BODY",BODY,{"disambiguationData":[OSD([sQuery(id+"F19.wireOp",EDGE,"E24.bottom"),sQuery(id+"F19.wireOp",EDGE,"E24.top"),sQuery(id+"F19.wireOp",EDGE,"E24.left"),sQuery(id+"F19.wireOp",EDGE,"E24.right")])]})])],"isStart":false})]});}
            var sketch = newSketch(context, id + "F27", { "sketchPlane" : qUnion([Q0])});
            skLineSegment(sketch, "E31", {"start": v(-18.95, 15.95) * mm, "end": v(18.95, -15.95) * mm, "construction": true});
            skLineSegment(sketch, "E32.bottom", {"start": v(-18.75, -15.75) * mm, "end": v(18.75, -15.75) * mm});
            skLineSegment(sketch, "E32.top", {"start": v(-18.75, 15.75) * mm, "end": v(18.75, 15.75) * mm});
            skLineSegment(sketch, "E32.left", {"start": v(-18.75, -15.75) * mm, "end": v(-18.75, 15.75) * mm});
            skLineSegment(sketch, "E32.right", {"start": v(18.75, -15.75) * mm, "end": v(18.75, 15.75) * mm});
            skPoint(sketch, "E32.middle", {"position": v(0, 0) * mm});
            skSolve(sketch);
        }
        {
            var Q0;
            Q0=makeQuery(id+"F27.imprint","IMPRINT",FACE,{"disambiguationData":[TD([[makeQuery(id+"F27.imprint","IMPRINT",EDGE,{"derivedFrom":sQuery(id+"F27.wireOp",EDGE,"E32.bottom")}),1.0]])]});
            extrude(context, id + "F28", {"entities" : qUnion([Q0]), "oppositeDirection" : true, "depth" : 1.05 * mm});
        }
        {
            var Q0;
            Q0=makeQuery(id+"F16.boolean.opBoolean","COPY",FACE,{"derivedFrom":makeQuery(id+"F16.opExtrude","CAP_FACE",FACE,{"disambiguationData":[OSD([sQuery(id+"F2.wireOp",EDGE,"E1.top"),sQuery(id+"F13.wireOp",EDGE,"E17"),sQuery(id+"F13.wireOp",EDGE,"E18"),sQuery(id+"F15.wireOp",EDGE,"E20")])],"isStart":false})});
            var sketch = newSketch(context, id + "F29", { "sketchPlane" : qUnion([Q0])});
            skLineSegment(sketch, "E33.bottom", {"start": v(-9.25, 15.95) * mm, "end": v(9.25, 15.95) * mm});
            skLineSegment(sketch, "E33.top", {"start": v(-9.25, 13.45) * mm, "end": v(9.25, 13.45) * mm});
            skLineSegment(sketch, "E33.left", {"start": v(-9.25, 15.95) * mm, "end": v(-9.25, 13.45) * mm});
            skLineSegment(sketch, "E33.right", {"start": v(9.25, 15.95) * mm, "end": v(9.25, 13.45) * mm});
            skSolve(sketch);
        }
        {
            var Q0;
            Q0=makeQuery(id+"F29.imprint","IMPRINT",FACE,{"disambiguationData":[TD([[makeQuery(id+"F29.imprint","IMPRINT",EDGE,{"derivedFrom":sQuery(id+"F29.wireOp",EDGE,"E33.bottom")}),-1.0]])]});
            extrude(context, id + "F30", {"entities" : qUnion([Q0]), "operationType" : NewBodyOperationType.REMOVE, "depth" : 25 * mm});
        }
        {
            var Q0;
            Q0=makeQuery(id+"F22.boolean.opBoolean","COPY",FACE,{"derivedFrom":makeQuery(id+"F22.opExtrude","CAP_FACE",FACE,{"disambiguationData":[OSD([sQuery(id+"F21.wireOp",EDGE,"E25.bottom"),sQuery(id+"F21.wireOp",EDGE,"E25.top"),sQuery(id+"F21.wireOp",EDGE,"E25.left"),sQuery(id+"F21.wireOp",EDGE,"E25.right")])],"isStart":false})});
            var sketch = newSketch(context, id + "F31", { "sketchPlane" : qUnion([Q0])});
            skCircle(sketch, "E34", {"center": v(-16.45, 13.95) * mm, "radius": 1.8 * mm});
            skSolve(sketch);
        }
        {
            var Q0;
            Q0=makeQuery(id+"F22.boolean.opBoolean","COPY",FACE,{"derivedFrom":makeQuery(id+"F22.opExtrude","CAP_FACE",FACE,{"disambiguationData":[OSD([sQuery(id+"F21.wireOp",EDGE,"E26.bottom"),sQuery(id+"F21.wireOp",EDGE,"E26.top"),sQuery(id+"F21.wireOp",EDGE,"E26.left"),sQuery(id+"F21.wireOp",EDGE,"E26.right")])],"isStart":false})});
            var sketch = newSketch(context, id + "F32", { "sketchPlane" : qUnion([Q0])});
            skCircle(sketch, "E35", {"center": v(16.45, 13.95) * mm, "radius": 1.8 * mm});
            skSolve(sketch);
        }
        {
            var Q0;
            Q0=makeQuery(id+"F32.imprint","IMPRINT",FACE,{"disambiguationData":[TD([[makeQuery(id+"F32.imprint","IMPRINT",EDGE,{"derivedFrom":makeQuery(id+"F26.boolean.opBoolean","COPY",EDGE,{"derivedFrom":makeQuery(id+"F26.opExtrude","CAP_EDGE",EDGE,{"disambiguationData":[OSD([sQuery(id+"F24.wireOp",EDGE,"E29")])],"isStart":true})})}),-1.0]])]});
            var Q1;
            {var subQ0=sQuery(id+"F32.wireOp",EDGE,"E35");var subQ1=makeQuery(id+"F22.boolean.opBoolean","COPY",EDGE,{"derivedFrom":makeQuery(id+"F22.opExtrude","CAP_EDGE",EDGE,{"disambiguationData":[OSD([sQuery(id+"F21.wireOp",EDGE,"E26.bottom")])],"isStart":false})});var subQ2=makeQuery(id+"F32.imprint","INTERSECT",VERTEX,{"disambiguationData":[OD(0.0)],"derivedFrom":[subQ1,subQ0]});Q1=makeQuery(id+"F32.imprint","IMPRINT",FACE,{"disambiguationData":[TD([[makeQuery(id+"F32.imprint","IMPRINT",EDGE,{"disambiguationData":[TD([[subQ2,-1.0]])],"derivedFrom":subQ0}),1.0]])]});}
            var Q2;
            Q2=makeQuery(id+"F28.opExtrude","CAP_FACE",FACE,{"disambiguationData":[OSD([sQuery(id+"F27.wireOp",EDGE,"E32.bottom"),sQuery(id+"F27.wireOp",EDGE,"E32.top"),sQuery(id+"F27.wireOp",EDGE,"E32.left"),sQuery(id+"F27.wireOp",EDGE,"E32.right")])],"isStart":false});
            extrude(context, id + "F33", {"entities" : qUnion([Q0, Q1]), "operationType" : NewBodyOperationType.ADD, "endBound" : BoundingType.UP_TO_SURFACE, "endBoundEntityFace" : qUnion([Q2]), "depth" : 25 * mm});
        }
        {
            var Q0;
            Q0=makeQuery(id+"F31.imprint","IMPRINT",FACE,{"disambiguationData":[TD([[makeQuery(id+"F31.imprint","IMPRINT",EDGE,{"derivedFrom":makeQuery(id+"F26.boolean.opBoolean","COPY",EDGE,{"derivedFrom":makeQuery(id+"F26.opExtrude","CAP_EDGE",EDGE,{"disambiguationData":[OSD([sQuery(id+"F23.wireOp",EDGE,"E28")])],"isStart":true})})}),-1.0]])]});
            var Q1;
            {var subQ0=sQuery(id+"F31.wireOp",EDGE,"E34");var subQ1=makeQuery(id+"F22.boolean.opBoolean","COPY",EDGE,{"derivedFrom":makeQuery(id+"F22.opExtrude","CAP_EDGE",EDGE,{"disambiguationData":[OSD([sQuery(id+"F21.wireOp",EDGE,"E25.bottom")])],"isStart":false})});var subQ2=makeQuery(id+"F31.imprint","INTERSECT",VERTEX,{"disambiguationData":[OD(0.0)],"derivedFrom":[subQ1,subQ0]});Q1=makeQuery(id+"F31.imprint","IMPRINT",FACE,{"disambiguationData":[TD([[makeQuery(id+"F31.imprint","IMPRINT",EDGE,{"disambiguationData":[TD([[subQ2,1.0]])],"derivedFrom":subQ0}),1.0]])]});}
            var Q2;
            Q2=makeQuery(id+"F28.opExtrude","CAP_FACE",FACE,{"disambiguationData":[OSD([sQuery(id+"F27.wireOp",EDGE,"E32.bottom"),sQuery(id+"F27.wireOp",EDGE,"E32.top"),sQuery(id+"F27.wireOp",EDGE,"E32.left"),sQuery(id+"F27.wireOp",EDGE,"E32.right")])],"isStart":false});
            extrude(context, id + "F34", {"entities" : qUnion([Q0, Q1]), "operationType" : NewBodyOperationType.ADD, "endBound" : BoundingType.UP_TO_SURFACE, "endBoundEntityFace" : qUnion([Q2]), "depth" : 25 * mm});
        }
        {
            var Q0;
            Q0=makeQuery(id+"F22.boolean.opBoolean","COPY",FACE,{"derivedFrom":makeQuery(id+"F22.opExtrude","CAP_FACE",FACE,{"disambiguationData":[OSD([sQuery(id+"F21.wireOp",EDGE,"E27.bottom"),sQuery(id+"F21.wireOp",EDGE,"E27.top"),sQuery(id+"F21.wireOp",EDGE,"E27.left"),sQuery(id+"F21.wireOp",EDGE,"E27.right")])],"isStart":false})});
            var sketch = newSketch(context, id + "F35", { "sketchPlane" : qUnion([Q0])});
            skCircle(sketch, "E36", {"center": v(16.45, -13.95) * mm, "radius": 1.8 * mm});
            skSolve(sketch);
        }
        {
            var Q0;
            {var subQ0=sQuery(id+"F35.wireOp",EDGE,"E36");var subQ1=makeQuery(id+"F22.boolean.opBoolean","COPY",EDGE,{"derivedFrom":makeQuery(id+"F22.opExtrude","CAP_EDGE",EDGE,{"disambiguationData":[OSD([sQuery(id+"F21.wireOp",EDGE,"E27.bottom")])],"isStart":false})});var subQ2=makeQuery(id+"F35.imprint","INTERSECT",VERTEX,{"disambiguationData":[OD(0.0)],"derivedFrom":[subQ1,subQ0]});Q0=makeQuery(id+"F35.imprint","IMPRINT",FACE,{"disambiguationData":[TD([[makeQuery(id+"F35.imprint","IMPRINT",EDGE,{"disambiguationData":[TD([[subQ2,1.0]])],"derivedFrom":subQ0}),1.0]])]});}
            var Q1;
            Q1=makeQuery(id+"F35.imprint","IMPRINT",FACE,{"disambiguationData":[TD([[makeQuery(id+"F35.imprint","IMPRINT",EDGE,{"derivedFrom":makeQuery(id+"F26.boolean.opBoolean","COPY",EDGE,{"derivedFrom":makeQuery(id+"F26.opExtrude","CAP_EDGE",EDGE,{"disambiguationData":[OSD([sQuery(id+"F25.wireOp",EDGE,"E30")])],"isStart":true})})}),-1.0]])]});
            var Q2;
            {var subQ0=sQuery(id+"F27.wireOp",EDGE,"E32.right");var subQ3=sQuery(id+"F27.wireOp",EDGE,"E32.left");var subQ5=sQuery(id+"F27.wireOp",EDGE,"E32.top");var subQ7=sQuery(id+"F27.wireOp",EDGE,"E32.bottom");var subQ8=makeQuery(id+"F28.opExtrude","SWEPT_FACE",FACE,{"disambiguationData":[OSD([subQ7])]});Q2=makeQuery(id+"F34.boolean.opBoolean","SPLIT",FACE,{"disambiguationData":[TD([subQ8])],"derivedFrom":makeQuery(id+"F33.boolean.opBoolean","SPLIT",FACE,{"disambiguationData":[TD([subQ8])],"derivedFrom":makeQuery(id+"F28.opExtrude","CAP_FACE",FACE,{"disambiguationData":[OSD([subQ7,subQ5,subQ3,subQ0])],"isStart":false})})});}
            extrude(context, id + "F36", {"entities" : qUnion([Q0, Q1]), "operationType" : NewBodyOperationType.ADD, "endBound" : BoundingType.UP_TO_SURFACE, "endBoundEntityFace" : qUnion([Q2]), "depth" : 25 * mm});
        }
        {
            var Q0;
            Q0=makeQuery(id+"F8.opExtrude","CAP_FACE",FACE,{"disambiguationData":[OSD([sQuery(id+"F6.wireOp",EDGE,"E13.bottom"),sQuery(id+"F6.wireOp",EDGE,"E13.top"),sQuery(id+"F6.wireOp",EDGE,"E13.left"),sQuery(id+"F6.wireOp",EDGE,"E13.right")])],"isStart":false});
            var sketch = newSketch(context, id + "F37", { "sketchPlane" : qUnion([Q0])});
            skCircle(sketch, "E37", {"center": v(-16.45, -13.95) * mm, "radius": 1.8 * mm});
            skSolve(sketch);
        }
        {
            var Q0;
            {var subQ0=sQuery(id+"F37.wireOp",EDGE,"E37");var subQ1=makeQuery(id+"F8.opExtrude","CAP_EDGE",EDGE,{"disambiguationData":[OSD([sQuery(id+"F6.wireOp",EDGE,"E13.top")])],"isStart":false});var subQ2=makeQuery(id+"F37.imprint","INTERSECT",VERTEX,{"disambiguationData":[OD(0.0)],"derivedFrom":[subQ1,subQ0]});Q0=makeQuery(id+"F37.imprint","IMPRINT",FACE,{"disambiguationData":[TD([[makeQuery(id+"F37.imprint","IMPRINT",EDGE,{"disambiguationData":[TD([[subQ2,-1.0]])],"derivedFrom":subQ0}),1.0]])]});}
            var Q1;
            Q1=makeQuery(id+"F37.imprint","IMPRINT",FACE,{"disambiguationData":[TD([[makeQuery(id+"F37.imprint","IMPRINT",EDGE,{"derivedFrom":makeQuery(id+"F11.boolean.opBoolean","COPY",EDGE,{"derivedFrom":makeQuery(id+"F11.opExtrude","CAP_EDGE",EDGE,{"disambiguationData":[OSD([sQuery(id+"F10.wireOp",EDGE,"E16")])],"isStart":true})})}),-1.0]])]});
            var Q2;
            {var subQ0=sQuery(id+"F27.wireOp",EDGE,"E32.right");var subQ3=sQuery(id+"F27.wireOp",EDGE,"E32.left");var subQ5=sQuery(id+"F27.wireOp",EDGE,"E32.top");var subQ7=sQuery(id+"F27.wireOp",EDGE,"E32.bottom");var subQ8=makeQuery(id+"F28.opExtrude","SWEPT_FACE",FACE,{"disambiguationData":[OSD([subQ7])]});Q2=makeQuery(id+"F36.boolean.opBoolean","SPLIT",FACE,{"disambiguationData":[TD([subQ8])],"derivedFrom":makeQuery(id+"F34.boolean.opBoolean","SPLIT",FACE,{"disambiguationData":[TD([subQ8])],"derivedFrom":makeQuery(id+"F33.boolean.opBoolean","SPLIT",FACE,{"disambiguationData":[TD([subQ8])],"derivedFrom":makeQuery(id+"F28.opExtrude","CAP_FACE",FACE,{"disambiguationData":[OSD([subQ7,subQ5,subQ3,subQ0])],"isStart":false})})})});}
            extrude(context, id + "F38", {"entities" : qUnion([Q0, Q1]), "operationType" : NewBodyOperationType.ADD, "endBound" : BoundingType.UP_TO_SURFACE, "endBoundEntityFace" : qUnion([Q2]), "depth" : 25 * mm, "hasSecondDirection" : true, "secondDirectionOppositeDirection" : false, "secondDirectionDepth" : 1.6 * mm});
        }
        {
            var Q0;
            {var subQ4=sQuery(id+"F27.wireOp",EDGE,"E32.bottom");var subQ5=makeQuery(id+"F28.opExtrude","SWEPT_FACE",FACE,{"disambiguationData":[OSD([subQ4])]});var subQ6=sQuery(id+"F27.wireOp",EDGE,"E32.top");var subQ8=sQuery(id+"F27.wireOp",EDGE,"E32.left");var subQ12=sQuery(id+"F27.wireOp",EDGE,"E32.right");Q0=makeQuery(id+"F38.boolean.opBoolean","SPLIT",FACE,{"disambiguationData":[TD([subQ5])],"derivedFrom":makeQuery(id+"F36.boolean.opBoolean","SPLIT",FACE,{"disambiguationData":[TD([subQ5])],"derivedFrom":makeQuery(id+"F34.boolean.opBoolean","SPLIT",FACE,{"disambiguationData":[TD([subQ5])],"derivedFrom":makeQuery(id+"F33.boolean.opBoolean","SPLIT",FACE,{"disambiguationData":[TD([subQ5])],"derivedFrom":makeQuery(id+"F28.opExtrude","CAP_FACE",FACE,{"disambiguationData":[OSD([subQ4,subQ6,subQ8,subQ12])],"isStart":false})})})})});}
            var sketch = newSketch(context, id + "F39", { "sketchPlane" : qUnion([Q0])});
            skLineSegment(sketch, "E38.bottom", {"start": v(-18.75, 15.75) * mm, "end": v(-13.75, 15.75) * mm});
            skLineSegment(sketch, "E38.top", {"start": v(-18.75, 10.75) * mm, "end": v(-13.75, 10.75) * mm});
            skLineSegment(sketch, "E38.left", {"start": v(-18.75, 15.75) * mm, "end": v(-18.75, 10.75) * mm});
            skLineSegment(sketch, "E38.right", {"start": v(-13.75, 15.75) * mm, "end": v(-13.75, 10.75) * mm});
            skLineSegment(sketch, "E39.bottom", {"start": v(18.75, 15.75) * mm, "end": v(13.75, 15.75) * mm});
            skLineSegment(sketch, "E39.top", {"start": v(18.75, 10.75) * mm, "end": v(13.75, 10.75) * mm});
            skLineSegment(sketch, "E39.left", {"start": v(18.75, 15.75) * mm, "end": v(18.75, 10.75) * mm});
            skLineSegment(sketch, "E39.right", {"start": v(13.75, 15.75) * mm, "end": v(13.75, 10.75) * mm});
            skLineSegment(sketch, "E40.bottom", {"start": v(18.75, -15.75) * mm, "end": v(13.75, -15.75) * mm});
            skLineSegment(sketch, "E40.top", {"start": v(18.75, -10.75) * mm, "end": v(13.75, -10.75) * mm});
            skLineSegment(sketch, "E40.left", {"start": v(18.75, -15.75) * mm, "end": v(18.75, -10.75) * mm});
            skLineSegment(sketch, "E40.right", {"start": v(13.75, -15.75) * mm, "end": v(13.75, -10.75) * mm});
            skLineSegment(sketch, "E41.bottom", {"start": v(-18.75, -15.75) * mm, "end": v(-13.75, -15.75) * mm});
            skLineSegment(sketch, "E41.top", {"start": v(-18.75, -10.75) * mm, "end": v(-13.75, -10.75) * mm});
            skLineSegment(sketch, "E41.left", {"start": v(-18.75, -15.75) * mm, "end": v(-18.75, -10.75) * mm});
            skLineSegment(sketch, "E41.right", {"start": v(-13.75, -15.75) * mm, "end": v(-13.75, -10.75) * mm});
            skSolve(sketch);
        }
        {
            var Q0;
            Q0 = qSketchRegion(id + "F39", true);
            extrude(context, id + "F40", {"entities" : qUnion([Q0]), "operationType" : NewBodyOperationType.ADD, "depth" : 2 * mm});
        }
        {
            var Q0;
            {var subQ0=sQuery(id+"F39.wireOp",EDGE,"E38.left");var subQ1=sQuery(id+"F39.wireOp",EDGE,"E38.top");var subQ2=sQuery(id+"F39.wireOp",EDGE,"E38.bottom");var subQ3=sQuery(id+"F39.wireOp",EDGE,"E38.right");Q0=makeQuery(id+"F40.boolean.opBoolean","SPLIT",FACE,{"disambiguationData":[TD([makeQuery(id+"F28.opExtrude","SWEPT_FACE",FACE,{"disambiguationData":[OSD([sQuery(id+"F27.wireOp",EDGE,"E32.bottom")])]})])],"derivedFrom":makeQuery(id+"F40.opExtrude","CAP_FACE",FACE,{"disambiguationData":[OSD([subQ2,subQ1,subQ0,subQ3])],"isStart":false})});}
            var sketch = newSketch(context, id + "F41", { "sketchPlane" : qUnion([Q0])});
            skLineSegment(sketch, "E42.bottom", {"start": v(-13.75, 10.75) * mm, "end": v(-18.75, 10.75) * mm});
            skLineSegment(sketch, "E42.top", {"start": v(-13.75, 15.75) * mm, "end": v(-18.75, 15.75) * mm});
            skLineSegment(sketch, "E42.left", {"start": v(-13.75, 10.75) * mm, "end": v(-13.75, 15.75) * mm});
            skLineSegment(sketch, "E42.right", {"start": v(-18.75, 10.75) * mm, "end": v(-18.75, 15.75) * mm});
            skSolve(sketch);
        }
        {
            var Q0;
            Q0 = qSketchRegion(id + "F41", true);
            extrude(context, id + "F42", {"entities" : qUnion([Q0]), "operationType" : NewBodyOperationType.ADD, "depth" : 1.9 * mm});
        }
        {
            var Q0;
            Q0=makeQuery(id+"F40.boolean.opBoolean","SPLIT",FACE,{"disambiguationData":[TD([makeQuery(id+"F33.opExtrude","SWEPT_FACE",FACE,{"disambiguationData":[OSD([sQuery(id+"F24.wireOp",EDGE,"E29")])]})])],"derivedFrom":makeQuery(id+"F40.opExtrude","CAP_FACE",FACE,{"disambiguationData":[OSD([sQuery(id+"F39.wireOp",EDGE,"E40.bottom"),sQuery(id+"F39.wireOp",EDGE,"E40.top"),sQuery(id+"F39.wireOp",EDGE,"E40.left"),sQuery(id+"F39.wireOp",EDGE,"E40.right")])],"isStart":false})});
            var Q1;
            Q1=makeQuery(id+"F40.boolean.opBoolean","SPLIT",FACE,{"disambiguationData":[TD([makeQuery(id+"F34.opExtrude","SWEPT_FACE",FACE,{"disambiguationData":[OSD([sQuery(id+"F23.wireOp",EDGE,"E28")])]})])],"derivedFrom":makeQuery(id+"F40.opExtrude","CAP_FACE",FACE,{"disambiguationData":[OSD([sQuery(id+"F39.wireOp",EDGE,"E41.bottom"),sQuery(id+"F39.wireOp",EDGE,"E41.top"),sQuery(id+"F39.wireOp",EDGE,"E41.left"),sQuery(id+"F39.wireOp",EDGE,"E41.right")])],"isStart":false})});
            var Q2;
            Q2=makeQuery(id+"F42.boolean.opBoolean","SPLIT",FACE,{"disambiguationData":[TD([makeQuery(id+"F38.opExtrude","SWEPT_FACE",FACE,{"disambiguationData":[OSD([sQuery(id+"F10.wireOp",EDGE,"E16")])]})])],"derivedFrom":makeQuery(id+"F42.opExtrude","CAP_FACE",FACE,{"disambiguationData":[OSD([sQuery(id+"F41.wireOp",EDGE,"E42.bottom"),sQuery(id+"F41.wireOp",EDGE,"E42.top"),sQuery(id+"F41.wireOp",EDGE,"E42.left"),sQuery(id+"F41.wireOp",EDGE,"E42.right")])],"isStart":false})});
            var Q3;
            Q3=makeQuery(id+"F40.boolean.opBoolean","SPLIT",FACE,{"disambiguationData":[TD([makeQuery(id+"F36.opExtrude","SWEPT_FACE",FACE,{"disambiguationData":[OSD([sQuery(id+"F25.wireOp",EDGE,"E30")])]})])],"derivedFrom":makeQuery(id+"F40.opExtrude","CAP_FACE",FACE,{"disambiguationData":[OSD([sQuery(id+"F39.wireOp",EDGE,"E39.bottom"),sQuery(id+"F39.wireOp",EDGE,"E39.top"),sQuery(id+"F39.wireOp",EDGE,"E39.left"),sQuery(id+"F39.wireOp",EDGE,"E39.right")])],"isStart":false})});
            extrude(context, id + "F43", {"entities" : qUnion([Q0, Q1, Q2, Q3]), "operationType" : NewBodyOperationType.REMOVE, "oppositeDirection" : true, "depth" : 25 * mm});
        }
        {
            var Q0;
            Q0=makeQuery(id+"F28.opExtrude","CAP_FACE",FACE,{"disambiguationData":[OSD([sQuery(id+"F27.wireOp",EDGE,"E32.bottom"),sQuery(id+"F27.wireOp",EDGE,"E32.top"),sQuery(id+"F27.wireOp",EDGE,"E32.left"),sQuery(id+"F27.wireOp",EDGE,"E32.right")])],"isStart":true});
            var sketch = newSketch(context, id + "F44", { "sketchPlane" : qUnion([Q0])});
            skCircle(sketch, "E43", {"center": v(16.45, 13.95) * mm, "radius": 2 * mm});
            skCircle(sketch, "E44", {"center": v(-16.45, 13.95) * mm, "radius": 2 * mm});
            skCircle(sketch, "E45", {"center": v(-16.45, -13.95) * mm, "radius": 2 * mm});
            skCircle(sketch, "E46", {"center": v(16.45, -13.95) * mm, "radius": 2 * mm});
            skSolve(sketch);
        }
        {
            var Q0;
            {var subQ0=sQuery(id+"F44.wireOp",EDGE,"E46");var subQ1=sQuery(id+"F27.wireOp",EDGE,"E32.bottom");var subQ2=makeQuery(id+"F28.opExtrude","CAP_EDGE",EDGE,{"disambiguationData":[OSD([subQ1])],"isStart":true});var subQ3=makeQuery(id+"F44.imprint","INTERSECT",VERTEX,{"disambiguationData":[OD(0.0)],"derivedFrom":[subQ2,subQ0]});Q0=makeQuery(id+"F44.imprint","IMPRINT",FACE,{"disambiguationData":[TD([[makeQuery(id+"F44.imprint","IMPRINT",EDGE,{"disambiguationData":[TD([[subQ3,-1.0]])],"derivedFrom":subQ0}),1.0]])]});}
            var Q1;
            {var subQ0=sQuery(id+"F44.wireOp",EDGE,"E45");var subQ1=sQuery(id+"F27.wireOp",EDGE,"E32.bottom");var subQ2=makeQuery(id+"F28.opExtrude","CAP_EDGE",EDGE,{"disambiguationData":[OSD([subQ1])],"isStart":true});var subQ3=makeQuery(id+"F44.imprint","INTERSECT",VERTEX,{"disambiguationData":[OD(0.0)],"derivedFrom":[subQ2,subQ0]});Q1=makeQuery(id+"F44.imprint","IMPRINT",FACE,{"disambiguationData":[TD([[makeQuery(id+"F44.imprint","IMPRINT",EDGE,{"disambiguationData":[TD([[subQ3,1.0]])],"derivedFrom":subQ0}),1.0]])]});}
            var Q2;
            {var subQ1=sQuery(id+"F27.wireOp",EDGE,"E32.left");var subQ2=sQuery(id+"F27.wireOp",EDGE,"E32.top");var subQ3=makeQuery(id+"F28.opExtrude","CAP_FACE",FACE,{"disambiguationData":[OSD([sQuery(id+"F27.wireOp",EDGE,"E32.bottom"),subQ2,subQ1,sQuery(id+"F27.wireOp",EDGE,"E32.right")])],"isStart":true});Q2=makeQuery(id+"F44.imprint","IMPRINT",FACE,{"disambiguationData":[TD([[makeQuery(id+"F44.imprint","IMPRINT",EDGE,{"derivedFrom":makeQuery(id+"F43.boolean.opBoolean","INTERSECT",EDGE,{"derivedFrom":[subQ3,makeQuery(id+"F43.opExtrude","SWEPT_FACE",FACE,{"disambiguationData":[OSD([sQuery(id+"F23.wireOp",EDGE,"E28"),sQuery(id+"F39.wireOp",EDGE,"E41.bottom"),sQuery(id+"F39.wireOp",EDGE,"E41.top"),sQuery(id+"F39.wireOp",EDGE,"E41.left"),sQuery(id+"F39.wireOp",EDGE,"E41.right")])]})]})}),-1.0]])]});}
            var Q3;
            {var subQ1=sQuery(id+"F27.wireOp",EDGE,"E32.right");var subQ2=sQuery(id+"F27.wireOp",EDGE,"E32.top");var subQ3=makeQuery(id+"F28.opExtrude","CAP_FACE",FACE,{"disambiguationData":[OSD([sQuery(id+"F27.wireOp",EDGE,"E32.bottom"),subQ2,sQuery(id+"F27.wireOp",EDGE,"E32.left"),subQ1])],"isStart":true});Q3=makeQuery(id+"F44.imprint","IMPRINT",FACE,{"disambiguationData":[TD([[makeQuery(id+"F44.imprint","IMPRINT",EDGE,{"derivedFrom":makeQuery(id+"F43.boolean.opBoolean","INTERSECT",EDGE,{"derivedFrom":[subQ3,makeQuery(id+"F43.opExtrude","SWEPT_FACE",FACE,{"disambiguationData":[OSD([sQuery(id+"F24.wireOp",EDGE,"E29"),sQuery(id+"F39.wireOp",EDGE,"E40.bottom"),sQuery(id+"F39.wireOp",EDGE,"E40.top"),sQuery(id+"F39.wireOp",EDGE,"E40.left"),sQuery(id+"F39.wireOp",EDGE,"E40.right")])]})]})}),-1.0]])]});}
            extrude(context, id + "F45", {"entities" : qUnion([Q0, Q1, Q2, Q3]), "operationType" : NewBodyOperationType.REMOVE, "oppositeDirection" : true, "depth" : 2.1 * mm});
        }
        {
            var Q0;
            {var subQ4=sQuery(id+"F27.wireOp",EDGE,"E32.bottom");var subQ5=makeQuery(id+"F28.opExtrude","SWEPT_FACE",FACE,{"disambiguationData":[OSD([subQ4])]});var subQ6=sQuery(id+"F27.wireOp",EDGE,"E32.top");var subQ8=sQuery(id+"F27.wireOp",EDGE,"E32.left");var subQ12=sQuery(id+"F27.wireOp",EDGE,"E32.right");Q0=makeQuery(id+"F38.boolean.opBoolean","SPLIT",FACE,{"disambiguationData":[TD([subQ5])],"derivedFrom":makeQuery(id+"F36.boolean.opBoolean","SPLIT",FACE,{"disambiguationData":[TD([subQ5])],"derivedFrom":makeQuery(id+"F34.boolean.opBoolean","SPLIT",FACE,{"disambiguationData":[TD([subQ5])],"derivedFrom":makeQuery(id+"F33.boolean.opBoolean","SPLIT",FACE,{"disambiguationData":[TD([subQ5])],"derivedFrom":makeQuery(id+"F28.opExtrude","CAP_FACE",FACE,{"disambiguationData":[OSD([subQ4,subQ6,subQ8,subQ12])],"isStart":false})})})})});}
            var sketch = newSketch(context, id + "F46", { "sketchPlane" : qUnion([Q0])});
            skLineSegment(sketch, "E47.bottom", {"start": v(9.25, -13.45) * mm, "end": v(-9.25, -13.45) * mm});
            skLineSegment(sketch, "E47.top", {"start": v(9.25, -11.95) * mm, "end": v(-9.25, -11.95) * mm});
            skLineSegment(sketch, "E47.left", {"start": v(9.25, -13.45) * mm, "end": v(9.25, -11.95) * mm});
            skLineSegment(sketch, "E47.right", {"start": v(-9.25, -13.45) * mm, "end": v(-9.25, -11.95) * mm});
            skSolve(sketch);
        }
        {
            var Q0;
            Q0=makeQuery(id+"F46.imprint","IMPRINT",FACE,{"disambiguationData":[TD([[makeQuery(id+"F46.imprint","IMPRINT",EDGE,{"derivedFrom":sQuery(id+"F46.wireOp",EDGE,"E47.bottom")}),-1.0]])]});
            extrude(context, id + "F47", {"entities" : qUnion([Q0]), "operationType" : NewBodyOperationType.ADD, "depth" : 1.5 * mm});
        }
    });
